# Revit family: HERZ Backflow Preventer 2623
name_source: partatom
category: Rohrzubehör
units: mm (PartAtom-declared; Revit-internal decimal feet)

## family parameters
Arbeitsebenenbasiert = Nein
Beim Laden mit Abzugskörper schneiden = Nein
Bemaßung runder Anschluss = Durchmesser verwenden
Gemeinsam genutzt = Nein
Immer vertikal = Ja
OmniClass-Nummer = 23.65.55.14
OmniClass-Titel = Valves for Liquid Services
Teiletyp = Unterbricht

## types (1)
- HERZ Backflow Preventer 2623
    Application = The check valve is suitable for central heating systems to prevent backflow.
This product can be used, in general, with different media, but liquids must be clear.
The valve can be used in any position.
The flow direction is indicated by an arrow on the body.
The check valve is spring-loaded by means of an axial guide and can be operated both at low and at high pressures.
Two bores 1/4“ plugs are fitted for measuring purposes.
    Body = forged brass according to EN 12420
    Check valve = POM (body), NBR (O-Ring), stainless steel AISI 302 (spring)
    End fitting = forged brass
    Female thread = acc. to ISO 228
    H02 = 2 mm  [stored 0.00656168 ft]
    Hersteller = HERZ Armaturen Ges.m.b.H.
    Male thread = acc. to ISO 228
    Max. operating pressure = 1600000.0 Pa
    Max. operating temperature = 95 °C
    Medium = clear liquids
    Min. operating temperature = -10 °C
    Min. operating temperature (water) = 1 °C
    Note = Pursuant to Article 33 of the REACH Regulation (EC No. 1907/2006), we are obliged to point out that the material lead is listed on the SVHC list and that all brass components manufactured in our products exceed 0.1% (w / w) lead (CAS: 7439-92-1 / EINECS: 231-100-4).
Since lead is a component part of an alloy, actual exposure is not possible and therefore no additional information on safe use is necessary.
    Plugs = brass
    R01 = 9 mm  [stored 0.0295276 ft]
    S03 = 10 mm  [stored 0.0328084 ft]
    SCTWCODE = 04;14;02
    SCTWSEQ = FW;SBT_TYP_FW="108";2
    SC_NennweiteBerechnet = 0
    Sealing = EPDM
    URL = www.herzvalves.com
    Vorgabe-Ansicht = 0 mm  [stored 0 ft]
    W01 = 45.00°

note: [stored X ft] marks values corroborated as IEEE doubles in the binary element streams (Revit-internal decimal feet)
